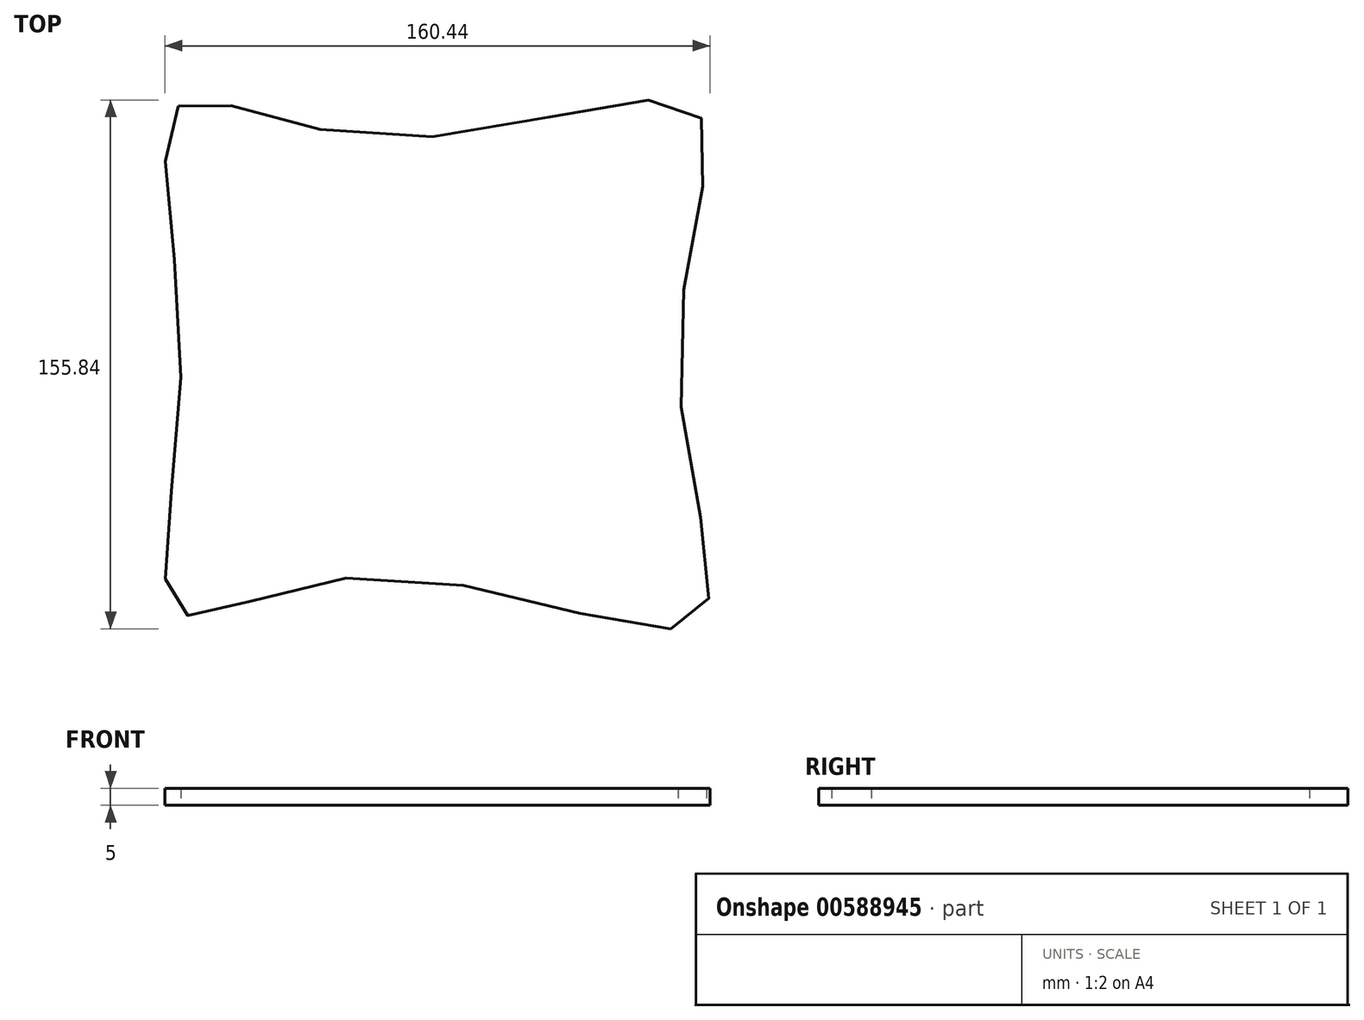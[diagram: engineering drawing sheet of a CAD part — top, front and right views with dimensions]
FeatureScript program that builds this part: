
annotation { "Feature Type Name" : "Feature", "Feature Type Description" : "" }
export const myFeature = defineFeature(function(context is Context, id is Id, definition is map)
    precondition{}
    {
        {
            var Q0;
            Q0=qCreatedBy(makeId("Top.planeOp"),FACE);
            var sketch = newSketch(context, id + "F0", { "sketchPlane" : qUnion([Q0])});
            skFitSpline(sketch, "E0", {"points": [v(-76.17, 75.36) * mm, v(-15.18, 65.93) * mm, v(75.78, 74.45) * mm, v(71.11, 0) * mm, v(76.6, -76.5) * mm, v(-18.77, -63.24) * mm, v(-76.55, -73.51) * mm, v(-75.35, 0) * mm, v(-76.17, 75.36) * mm]});
            skSolve(sketch);
        }
        {
            var Q0;
            Q0=makeQuery(id+"F0.imprint","IMPRINT",FACE,{"disambiguationData":[TD([[makeQuery(id+"F0.imprint","IMPRINT",EDGE,{"derivedFrom":sQuery(id+"F0.wireOp",EDGE,"E0")}),-1.0]])]});
            extrude(context, id + "F1", {"entities" : qUnion([Q0]), "depth" : 5 * mm, "offsetDistance" : 25.4 * mm});
        }
    });
